# Revit family: 0046370
name_source: partatom
category: Lighting Fixtures
revit_build: Autodesk Revit 2017 (Build: 20190507_1515(x64)
units: mm (PartAtom-declared; Revit-internal decimal feet)

## family parameters
Cut with Voids When Loaded = No
Host = Face
Light Source = Yes
OmniClass Number = 23.80.70.00
OmniClass Title = Lighting
Part Type = Normal
Room Calculation Point = No
Round Connector Dimension = Use Diameter
Shared = No

## types (4) — shared parameters
Apparent Load = 0 VA
Assembly Code = D5020200
AssetType = Fixed
ClassificationName = Uniclass2015
ClassificationValue = EF_70_80
Color Filter = 16777215
Default Elevation = 1219 mm
Dimming Lamp Color Temperature Shift = <None>
DocumentationLiterature = http://www.sylvania-lighting.com
ElectricShockClassification = Class I
Emit Shape Visible in Rendering = No
Emit from Circle Diameter = 610 mm
IfcExportAs = IfcLightFixtureType
IfcExportType = IfcLightFixtureType
ImpactProtectionIndex = IK08
IngressProtection = IP65
Keynote = 16500
LAM_D_SYL = 33 mm
LENGHT1_SYL = 546 mm
LENGHT_-1_SYL = -546 mm
Lamp = LED
LampColourRenderingIndex = 80
LampsType = LED
MID_W_DIST_SYL = 47 mm  [stored 0.154199 ft]
Manufacturer = Feilo Sylvania
ManufacturerName = Feilo Sylvania
Material_1_SYL = <By Category>
Material_2_SYL = <By Category>
Material_3_SYL = <By Category>
Material_4_SYL = <By Category>
NominalDepth = 67 mm
NominalHeight = 65 mm
NominalLength = 1122 mm
Tilt Angle = -90.00°
Type Image = <None>
URL = http://www.sylvania-lighting.com
Voltage = 0 V
Weight = 9.27 kg
zero-valued in all types: Cost, PowerFactor

## per-type parameters (varying)
| type | Description | LampColourTemperature | LampNominalLuminous | LuminousEfficacy | Model | ModelNumber | ModelReference | Name | Photometric Web File | TypeName |
| 0046374 ST WTRPRF SLIM 1200 IP65 2500LM 865 | START Waterproof Slim is a LED integrated polycarbonate housing luminaire with easy to access electrical terminal through bayonet lock end caps and tool-free electrical connection due to push-in terminal. Flexible installation as mounting brackets can be positioned freely on the luminaire. 19W; 2500lm; High efficiency with 132lm/W and 100,000 hours lifespan L70B50. SDCM < 5; IP65; IK08; Class I; 1207mm x 70mm x 69mm. | 6500 K | 2500 lm | 132 lm/W | START Waterproof Slim 1200 IP65 2500lm 865 | 0046374 | START Waterproof Slim 1200 IP65 2500lm 865 | START Waterproof Slim 1200 IP65 2500lm 865 | 0046374.ies | START Waterproof Slim 1200 IP65 2500lm 865 |
| 0046370 ST WTRPRF SLIM 1200 IP65 4600LM 840 | START Waterproof Slim is a LED integrated polycarbonate housing luminaire with easy to access electrical terminal through bayonet lock end caps and tool-free electrical connection due to push-in terminal. Flexible installation as mounting brackets can be positioned freely on the luminaire. 35W; 4600lm; High efficiency with 131lm/W and 100,000 hours lifespan L70B50. SDCM < 5; IP65; IK08; Class I; 1207mm x 70mm x 69mm. | 4000 K | 4600 lm | 131 lm/W | START Waterproof Slim 1200 IP65 4600lm 840 | 0046370 | START Waterproof Slim 1200 IP65 4600lm 840 | START Waterproof Slim 1200 IP65 4600lm 840 | 0046370.ies | START Waterproof Slim 1200 IP65 4600lm 840 |
| 0046369 ST WTRPRF SLIM 1200 IP65 2500LM 840 | START Waterproof Slim is a LED integrated polycarbonate housing luminaire with easy to access electrical terminal through bayonet lock end caps and tool-free electrical connection due to push-in terminal. Flexible installation as mounting brackets can be positioned freely on the luminaire. 19W; 2500lm; High efficiency with 132lm/W and 100,000 hours lifespan L70B50. SDCM < 5; IP65; IK08; Class I; 1207mm x 70mm x 69mm. | 4000 K | 2500 lm | 132 lm/W | START Waterproof Slim 1200 IP65 2500lm 840 | 0046369 | START Waterproof Slim 1200 IP65 2500lm 840 | START Waterproof Slim 1200 IP65 2500lm 840 | 0046369.ies | START Waterproof Slim 1200 IP65 2500lm 840 |
| 0046375 ST WTRPRF SLIM 1200 IP65 4600LM 865 | START Waterproof Slim is a LED integrated polycarbonate housing luminaire with easy to access electrical terminal through bayonet lock end caps and tool-free electrical connection due to push-in terminal. Flexible installation as mounting brackets can be positioned freely on the luminaire. 35W; 4600lm; High efficiency with 131lm/W and 100,000 hours lifespan L70B50. SDCM < 5; IP65; IK08; Class I; 1207mm x 70mm x 69mm. | 6500 K | 4600 lm | 131 lm/W | START Waterproof Slim 1200 IP65 4600lm 865 | 0046375 | START Waterproof Slim 1200 IP65 4600lm 865 | START Waterproof Slim 1200 IP65 4600lm 865 | 0046375.ies | START Waterproof Slim 1200 IP65 4600lm 865 |

note: [stored X ft] marks values corroborated as IEEE doubles in the binary element streams (Revit-internal decimal feet)

## geometry (parser evidence)
native form markers: Sweep x3
no freeform markers — native parametric forms only
